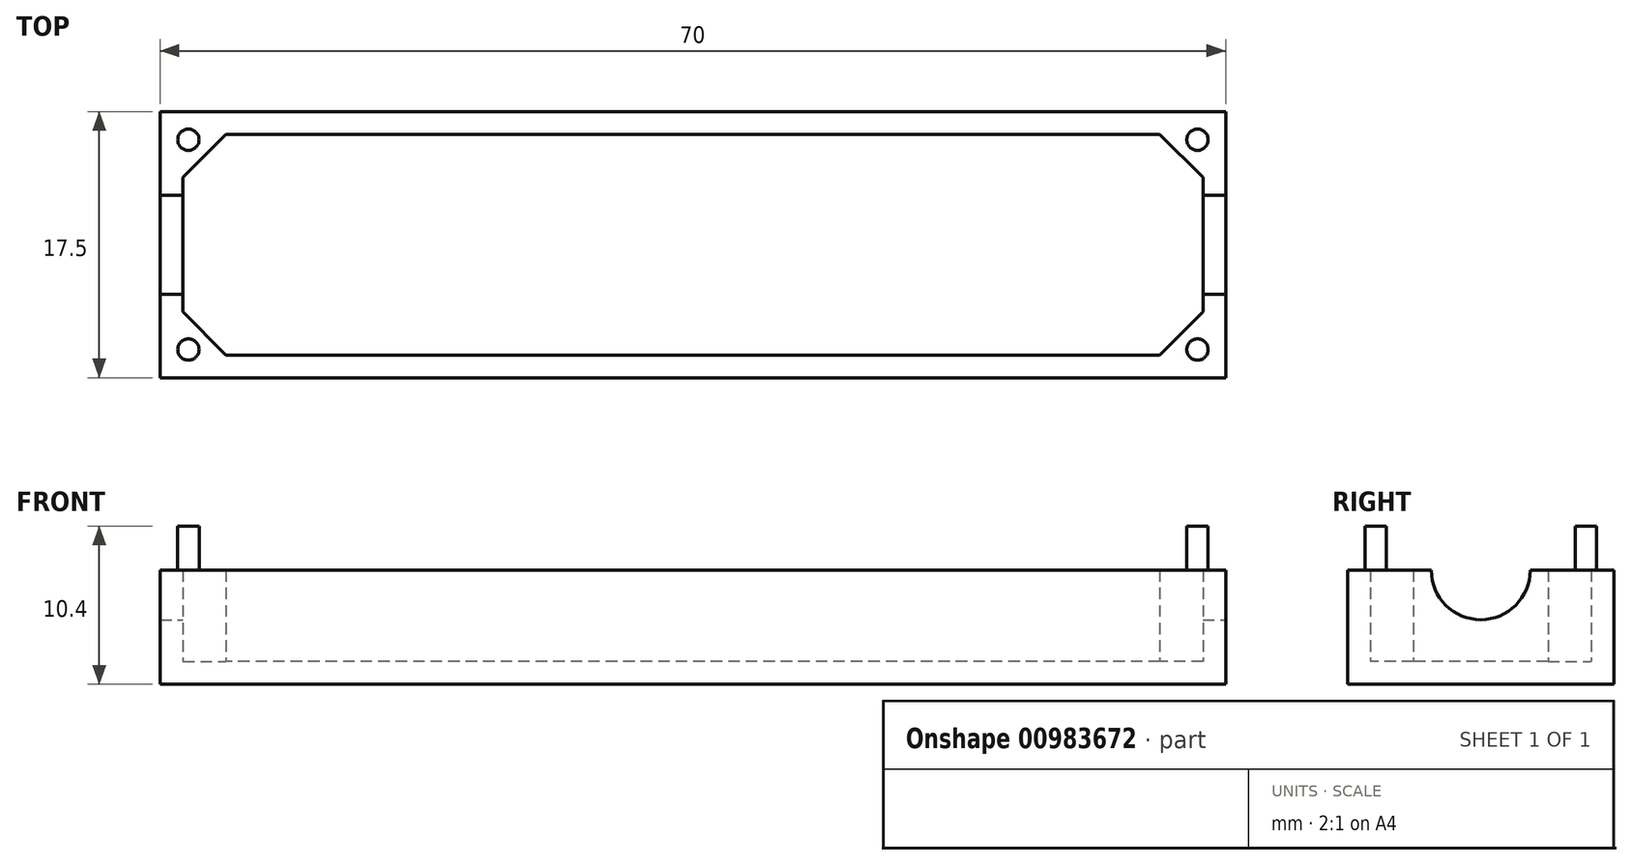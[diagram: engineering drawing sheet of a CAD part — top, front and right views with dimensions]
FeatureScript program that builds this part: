
annotation { "Feature Type Name" : "Feature", "Feature Type Description" : "" }
export const myFeature = defineFeature(function(context is Context, id is Id, definition is map)
    precondition{}
    {
        {
            var Q0;
            Q0=qCreatedBy(makeId("Top.planeOp"),FACE);
            var sketch = newSketch(context, id + "F0", { "sketchPlane" : qUnion([Q0])});
            skLineSegment(sketch, "E0.bottom", {"start": v(35, 8.75) * mm, "end": v(-35, 8.75) * mm});
            skLineSegment(sketch, "E0.top", {"start": v(35, -8.75) * mm, "end": v(-35, -8.75) * mm});
            skLineSegment(sketch, "E0.left", {"start": v(35, 8.75) * mm, "end": v(35, -8.75) * mm});
            skLineSegment(sketch, "E0.right", {"start": v(-35, 8.75) * mm, "end": v(-35, -8.75) * mm});
            skPoint(sketch, "E0.middle", {"position": v(0, 0) * mm});
            skSolve(sketch);
        }
        {
            var Q0;
            Q0=qSketchRegion(id+"F0",true);
            extrude(context, id + "F1", {"entities" : qUnion([Q0]), "depth" : 7.5 * mm, "offsetDistance" : 25.4 * mm});
        }
        {
            var Q0;
            Q0=makeQuery(id+"F1.opExtrude","CAP_FACE",FACE,{"disambiguationData":[OSD([sQuery(id+"F0.wireOp",EDGE,"E0.bottom"),sQuery(id+"F0.wireOp",EDGE,"E0.top"),sQuery(id+"F0.wireOp",EDGE,"E0.left"),sQuery(id+"F0.wireOp",EDGE,"E0.right")])],"isStart":false});
            shell(context, id + "F2", {"entities" : qUnion([Q0]), "thickness" : 1.5 * mm});
        }
        {
            var Q0;
            Q0=makeQuery(id+"F2.opShell","OFFSET_FACE",FACE,{"disambiguationData":[OSD([sQuery(id+"F0.wireOp",EDGE,"E0.bottom"),sQuery(id+"F0.wireOp",EDGE,"E0.top"),sQuery(id+"F0.wireOp",EDGE,"E0.left"),sQuery(id+"F0.wireOp",EDGE,"E0.right")])]});
            var sketch = newSketch(context, id + "F3", { "sketchPlane" : qUnion([Q0])});
            skLineSegment(sketch, "E1", {"start": v(-33.5, 4.42) * mm, "end": v(-30.67, 7.25) * mm});
            skLineSegment(sketch, "E2", {"start": v(-30.67, 7.25) * mm, "end": v(-33.5, 7.25) * mm});
            skLineSegment(sketch, "E3", {"start": v(-33.5, 7.25) * mm, "end": v(-33.5, 4.42) * mm});
            skLineSegment(sketch, "E4", {"start": v(0, 0) * mm, "end": v(0, 7.25) * mm});
            skLineSegment(sketch, "E5.MirrorCS", {"start": v(33.5, 4.42) * mm, "end": v(30.67, 7.25) * mm});
            skLineSegment(sketch, "E6.MirrorCS", {"start": v(30.67, 7.25) * mm, "end": v(33.5, 7.25) * mm});
            skLineSegment(sketch, "E7.MirrorCS", {"start": v(33.5, 7.25) * mm, "end": v(33.5, 4.42) * mm});
            skLineSegment(sketch, "E8", {"start": v(0, 0) * mm, "end": v(33.5, 0) * mm});
            skLineSegment(sketch, "E9.MirrorCS", {"start": v(33.5, -4.42) * mm, "end": v(30.67, -7.25) * mm});
            skLineSegment(sketch, "E10.MirrorCS", {"start": v(30.67, -7.25) * mm, "end": v(33.5, -7.25) * mm});
            skLineSegment(sketch, "E11.MirrorCS", {"start": v(33.5, -7.25) * mm, "end": v(33.5, -4.42) * mm});
            skLineSegment(sketch, "E12.MirrorCS", {"start": v(-33.5, -7.25) * mm, "end": v(-33.5, -4.42) * mm});
            skLineSegment(sketch, "E13.MirrorCS", {"start": v(-30.67, -7.25) * mm, "end": v(-33.5, -7.25) * mm});
            skLineSegment(sketch, "E14.MirrorCS", {"start": v(-33.5, -4.42) * mm, "end": v(-30.67, -7.25) * mm});
            skSolve(sketch);
        }
        {
            var Q0;
            Q0=qSketchRegion(id+"F3",true);
            var Q1;
            Q1=makeQuery(id+"F1.opExtrude","CAP_FACE",FACE,{"disambiguationData":[OSD([sQuery(id+"F0.wireOp",EDGE,"E0.bottom"),sQuery(id+"F0.wireOp",EDGE,"E0.top"),sQuery(id+"F0.wireOp",EDGE,"E0.left"),sQuery(id+"F0.wireOp",EDGE,"E0.right")])],"isStart":false});
            extrude(context, id + "F4", {"entities" : qUnion([Q0]), "operationType" : NewBodyOperationType.ADD, "endBound" : BoundingType.UP_TO_SURFACE, "depth" : 25 * mm, "endBoundEntityFace" : qUnion([Q1]), "offsetDistance" : 25 * mm});
        }
        {
            var Q0;
            Q0=makeQuery(id+"F4.boolean.opBoolean","MERGE",FACE,{"derivedFrom":[makeQuery(id+"F1.opExtrude","CAP_FACE",FACE,{"disambiguationData":[OSD([sQuery(id+"F0.wireOp",EDGE,"E0.bottom"),sQuery(id+"F0.wireOp",EDGE,"E0.top"),sQuery(id+"F0.wireOp",EDGE,"E0.left"),sQuery(id+"F0.wireOp",EDGE,"E0.right")])],"isStart":false}),makeQuery(id+"F4.opExtrude","CAP_FACE",FACE,{"disambiguationData":[OSD([sQuery(id+"F3.wireOp",EDGE,"E1"),sQuery(id+"F3.wireOp",EDGE,"E2"),sQuery(id+"F3.wireOp",EDGE,"E3")])],"isStart":false}),makeQuery(id+"F4.opExtrude","CAP_FACE",FACE,{"disambiguationData":[OSD([sQuery(id+"F3.wireOp",EDGE,"E7.MirrorCS"),sQuery(id+"F3.wireOp",EDGE,"E6.MirrorCS"),sQuery(id+"F3.wireOp",EDGE,"E5.MirrorCS")])],"isStart":false}),makeQuery(id+"F4.opExtrude","CAP_FACE",FACE,{"disambiguationData":[OSD([sQuery(id+"F3.wireOp",EDGE,"E9.MirrorCS"),sQuery(id+"F3.wireOp",EDGE,"E11.MirrorCS"),sQuery(id+"F3.wireOp",EDGE,"E10.MirrorCS")])],"isStart":false}),makeQuery(id+"F4.opExtrude","CAP_FACE",FACE,{"disambiguationData":[OSD([sQuery(id+"F3.wireOp",EDGE,"E12.MirrorCS"),sQuery(id+"F3.wireOp",EDGE,"E13.MirrorCS"),sQuery(id+"F3.wireOp",EDGE,"E14.MirrorCS")])],"isStart":false})]});
            var sketch = newSketch(context, id + "F5", { "sketchPlane" : qUnion([Q0])});
            skCircle(sketch, "E15", {"center": v(-33.15, 6.9) * mm, "radius": 0.7 * mm});
            skCircle(sketch, "E16", {"center": v(-33.15, -6.9) * mm, "radius": 0.7 * mm});
            skCircle(sketch, "E17", {"center": v(33.15, 6.9) * mm, "radius": 0.7 * mm});
            skCircle(sketch, "E18", {"center": v(33.15, -6.9) * mm, "radius": 0.7 * mm});
            skPoint(sketch, "E19.endSnap0", {"position": v(-32.09, 5.84) * mm});
            skLineSegment(sketch, "E20", {"start": v(-33.15, 6.9) * mm, "end": v(-32.09, 5.84) * mm});
            skLineSegment(sketch, "E21", {"start": v(-33.15, -6.9) * mm, "end": v(-32.09, -5.84) * mm});
            skLineSegment(sketch, "E22", {"start": v(33.15, -6.9) * mm, "end": v(32.09, -5.84) * mm});
            skLineSegment(sketch, "E23", {"start": v(33.15, 6.9) * mm, "end": v(32.09, 5.84) * mm});
            skSolve(sketch);
        }
        {
            var Q0;
            Q0=qSketchRegion(id+"F5",true);
            extrude(context, id + "F6", {"entities" : qUnion([Q0]), "operationType" : NewBodyOperationType.ADD, "depth" : 2.9 * mm, "offsetDistance" : 25 * mm});
        }
        {
            var Q0;
            Q0=makeQuery(id+"F1.opExtrude","SWEPT_FACE",FACE,{"disambiguationData":[OSD([sQuery(id+"F0.wireOp",EDGE,"E0.left")])]});
            var sketch = newSketch(context, id + "F7", { "sketchPlane" : qUnion([Q0])});
            skCircle(sketch, "E24", {"center": v(0, 7.5) * mm, "radius": 3.25 * mm});
            skSolve(sketch);
        }
        {
            var Q0;
            Q0=qSketchRegion(id+"F7",true);
            extrude(context, id + "F8", {"entities" : qUnion([Q0]), "operationType" : NewBodyOperationType.REMOVE, "endBound" : BoundingType.THROUGH_ALL, "oppositeDirection" : true, "depth" : 25 * mm, "offsetDistance" : 25 * mm});
        }
    });
